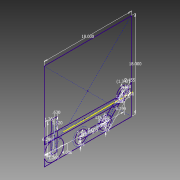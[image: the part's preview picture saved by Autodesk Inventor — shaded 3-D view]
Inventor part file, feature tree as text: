
AUTODESK INVENTOR PART (.ipt)
format: ipt  version: 2015 (Build 190159000, 159)  size: 109,056 bytes
history: native  units: in
note: dims shown in document units (in); Inventor stores cm internally (conversion verified against a paired STEP export)
features: sketch x1
ambient origin geometry x8: Origin, YZ Plane, XZ Plane, XY Plane, X Axis, Y Axis, Z Axis, Center Point
feature tree (1):
  sketch  "Sketch1"  dims[d0=5.0394in d1=1.063in d2=1.2598in d3=6.2992in d4=0.315in d5=0.6299in d6=0.6299in d7=135.0deg d8=0.315in d9=0.6299in d10=0.6299in d13=0.315in d14=2.455in d15=2.455in d16=1.2598in d17=16.378in d22=0.6299in d23=6.2992in d24=1.2598in d25=4.0in d26=0.6299in d27=0.6299in d29=2.5197in d31=0.3937in d32=0.3937in d34=2.455in d35=18.0in d36=18.0in d37=1.2598in d38=1.342in d40=1.2598in d41=1.2598in]
